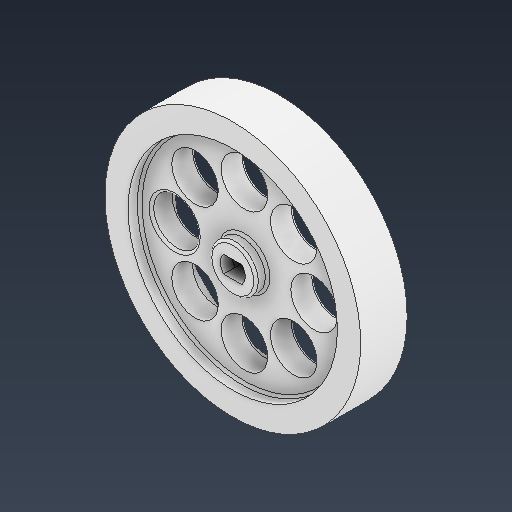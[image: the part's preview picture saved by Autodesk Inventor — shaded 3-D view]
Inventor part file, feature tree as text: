
AUTODESK INVENTOR PART (.ipt)
format: ipt  version: 2021 (Build 250183000, 183)  size: 245,760 bytes
history: mixed  units: mm
features: fillet x1, imported_body x1
ambient origin geometry x8: Origin, YZ Plane, XZ Plane, XY Plane, X Axis, Y Axis, Z Axis, Center Point
bodies: Solid1 (imported_parasolid)
feature tree (2):
  fillet  "Fillet4"  [1 undecoded]
  imported_body  NMx_Import_Brep_tag  [imported B-rep: ~40 faces, bbox_mm=[37.5, 30.0, 10.0]]
note: 1 required parameter value undecoded (feature->parameter linkage not recoverable at this tier; creation-order binding heuristic only, values carry confidence <= 0.55)
